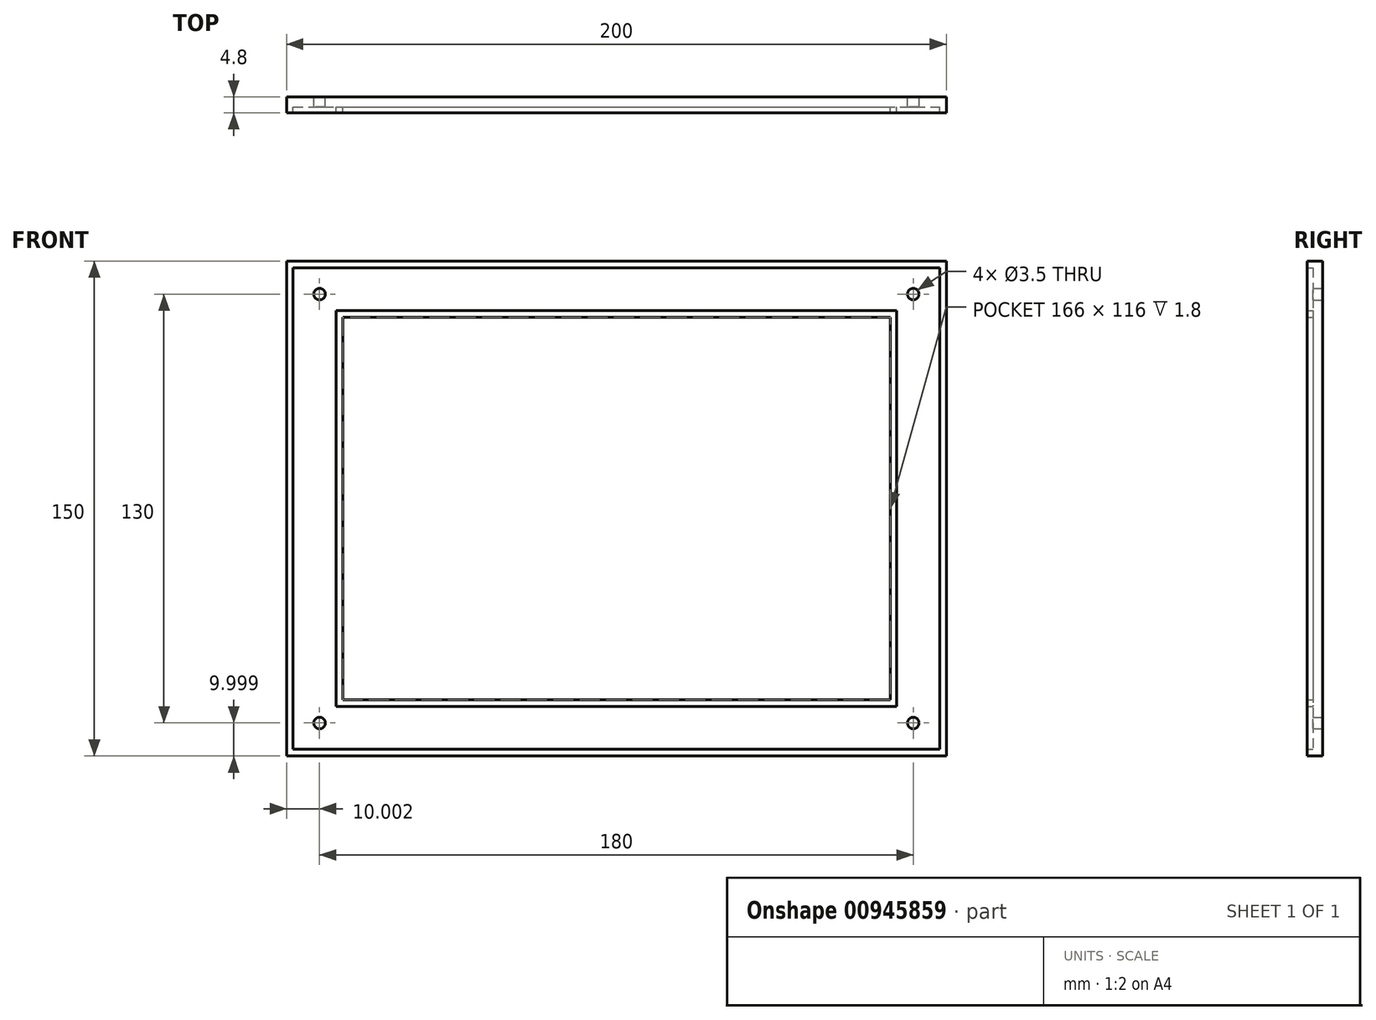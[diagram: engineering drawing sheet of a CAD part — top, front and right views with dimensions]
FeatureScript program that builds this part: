
annotation { "Feature Type Name" : "Feature", "Feature Type Description" : "" }
export const myFeature = defineFeature(function(context is Context, id is Id, definition is map)
    precondition{}
    {
        {
            var Q0;
            Q0=qCreatedBy(makeId("Front.planeOp"),FACE);
            var sketch = newSketch(context, id + "F0", { "sketchPlane" : qUnion([Q0])});
            skLineSegment(sketch, "E0.bottom", {"start": v(-91.96, 87.46) * mm, "end": v(108.04, 87.46) * mm});
            skLineSegment(sketch, "E0.top", {"start": v(-91.96, -62.54) * mm, "end": v(108.04, -62.54) * mm});
            skLineSegment(sketch, "E0.left", {"start": v(-91.96, 87.46) * mm, "end": v(-91.96, -62.54) * mm});
            skLineSegment(sketch, "E0.right", {"start": v(108.04, 87.46) * mm, "end": v(108.04, -62.54) * mm});
            skLineSegment(sketch, "E1.bottom", {"start": v(-81.96, 77.46) * mm, "end": v(98.04, 77.46) * mm, "construction": true});
            skLineSegment(sketch, "E1.top", {"start": v(-81.96, -52.54) * mm, "end": v(98.04, -52.54) * mm, "construction": true});
            skLineSegment(sketch, "E1.left", {"start": v(-81.96, 77.46) * mm, "end": v(-81.96, -52.54) * mm, "construction": true});
            skLineSegment(sketch, "E1.right", {"start": v(98.04, 77.46) * mm, "end": v(98.04, -52.54) * mm, "construction": true});
            skPoint(sketch, "E2", {"position": v(8.04, 87.46) * mm});
            skPoint(sketch, "E3", {"position": v(8.04, -52.54) * mm});
            skPoint(sketch, "E4", {"position": v(98.04, 12.46) * mm});
            skPoint(sketch, "E5", {"position": v(108.04, 12.46) * mm});
            skCircle(sketch, "E6", {"center": v(-81.96, 77.46) * mm, "radius": 1.75 * mm});
            skCircle(sketch, "E7", {"center": v(98.04, 77.46) * mm, "radius": 1.75 * mm});
            skCircle(sketch, "E8", {"center": v(98.04, -52.54) * mm, "radius": 1.75 * mm});
            skCircle(sketch, "E9", {"center": v(-81.96, -52.54) * mm, "radius": 1.75 * mm});
            skSolve(sketch);
        }
        {
            var Q0;
            Q0=makeQuery(id+"F0.imprint","IMPRINT",FACE,{"disambiguationData":[TD([[makeQuery(id+"F0.imprint","IMPRINT",EDGE,{"derivedFrom":sQuery(id+"F0.wireOp",EDGE,"E0.bottom")}),-1.0]])]});
            extrude(context, id + "F1", {"entities" : qUnion([Q0]), "depth" : 3 * mm, "offsetDistance" : 25 * mm});
        }
        {
            var Q0;
            Q0=makeQuery(id+"F1.opExtrude","CAP_FACE",FACE,{"disambiguationData":[OSD([sQuery(id+"F0.wireOp",EDGE,"E0.bottom"),sQuery(id+"F0.wireOp",EDGE,"E0.top"),sQuery(id+"F0.wireOp",EDGE,"E0.left"),sQuery(id+"F0.wireOp",EDGE,"E0.right"),sQuery(id+"F0.wireOp",EDGE,"E6"),sQuery(id+"F0.wireOp",EDGE,"E7"),sQuery(id+"F0.wireOp",EDGE,"E8"),sQuery(id+"F0.wireOp",EDGE,"E9")])],"isStart":false});
            var sketch = newSketch(context, id + "F2", { "sketchPlane" : qUnion([Q0])});
            skLineSegment(sketch, "E10.0.0", {"start": v(-91.96, 87.46) * mm, "end": v(-91.96, -62.54) * mm});
            skLineSegment(sketch, "E10.0.1", {"start": v(-91.96, -62.54) * mm, "end": v(108.04, -62.54) * mm});
            skLineSegment(sketch, "E10.0.2", {"start": v(108.04, -62.54) * mm, "end": v(108.04, 87.46) * mm});
            skLineSegment(sketch, "E10.0.3", {"start": v(108.04, 87.46) * mm, "end": v(-91.96, 87.46) * mm});
            skLineSegment(sketch, "E11.bottom", {"start": v(-89.96, 85.46) * mm, "end": v(106.04, 85.46) * mm});
            skLineSegment(sketch, "E11.top", {"start": v(-89.96, -60.54) * mm, "end": v(106.04, -60.54) * mm});
            skLineSegment(sketch, "E11.left", {"start": v(-89.96, 85.46) * mm, "end": v(-89.96, -60.54) * mm});
            skLineSegment(sketch, "E11.right", {"start": v(106.04, 85.46) * mm, "end": v(106.04, -60.54) * mm});
            skPoint(sketch, "E12", {"position": v(8.04, 85.46) * mm});
            skPoint(sketch, "E13", {"position": v(106.04, 12.46) * mm});
            skPoint(sketch, "E14", {"position": v(108.04, 12.46) * mm});
            skPoint(sketch, "E15", {"position": v(8.04, -62.54) * mm});
            skLineSegment(sketch, "E16.bottom", {"start": v(-76.96, 72.46) * mm, "end": v(93.04, 72.46) * mm});
            skLineSegment(sketch, "E16.top", {"start": v(-76.96, -47.54) * mm, "end": v(93.04, -47.54) * mm});
            skLineSegment(sketch, "E16.left", {"start": v(-76.96, 72.46) * mm, "end": v(-76.96, -47.54) * mm});
            skLineSegment(sketch, "E16.right", {"start": v(93.04, 72.46) * mm, "end": v(93.04, -47.54) * mm});
            skLineSegment(sketch, "E17.bottom", {"start": v(-74.96, 70.46) * mm, "end": v(91.04, 70.46) * mm});
            skLineSegment(sketch, "E17.top", {"start": v(-74.96, -45.54) * mm, "end": v(91.04, -45.54) * mm});
            skLineSegment(sketch, "E17.left", {"start": v(-74.96, 70.46) * mm, "end": v(-74.96, -45.54) * mm});
            skLineSegment(sketch, "E17.right", {"start": v(91.04, 70.46) * mm, "end": v(91.04, -45.54) * mm});
            skPoint(sketch, "E18", {"position": v(8.04, 70.46) * mm});
            skPoint(sketch, "E19", {"position": v(93.04, 12.46) * mm});
            skPoint(sketch, "E20", {"position": v(8.04, 72.46) * mm});
            skPoint(sketch, "E21", {"position": v(91.04, 12.46) * mm});
            skSolve(sketch);
        }
        {
            var Q0;
            Q0 = qSketchRegion(id + "F2", true);
            var Q1;
            Q1=makeQuery(id+"F2.imprint","IMPRINT",FACE,{"disambiguationData":[TD([[makeQuery(id+"F2.imprint","IMPRINT",EDGE,{"derivedFrom":sQuery(id+"F2.wireOp",EDGE,"E16.bottom")}),-1.0]])]});
            extrude(context, id + "F3", {"entities" : qUnion([Q0, Q1]), "operationType" : NewBodyOperationType.ADD, "depth" : 1.8 * mm, "offsetDistance" : 25 * mm});
        }
    });
